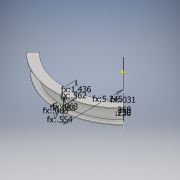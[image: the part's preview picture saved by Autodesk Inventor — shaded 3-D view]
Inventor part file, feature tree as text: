
AUTODESK INVENTOR PART (.ipt)
format: ipt  version: 2017 (Build 210142000, 142)  size: 168,448 bytes
history: native  units: in
note: dims shown in document units (in); Inventor stores cm internally (conversion verified against a paired STEP export)
features: sketch x5, extrude x4, revolve x1, plane x1
ambient origin geometry x8: Origin, YZ Plane, XZ Plane, XY Plane, X Axis, Y Axis, Z Axis, Center Point
bodies: Solid1 (feature_tree)
feature tree (11):
  revolve  "Revolution1"  [1 undecoded]
  plane  "Work Plane1"
  sketch  "Sketch2"  dims[d3=1.4364in d4=0.0625in]
  extrude  "Extrusion2"  Depth=0.0625in
  extrude  "Extrusion3"  TaperAngle=90.0deg  [1 undecoded]
  extrude  "Extrusion4"  Depth=0.375in
  extrude  "Extrusion5"  Depth=0.0312in TaperAngle=0.0deg
  sketch  "Sketch5"  dims[d11=0.3125in d12=1.0in d13=0.0in d14=0.0156in d15=0.0in d16=0.25in d17=0.0625in d18=0.0in d19=135.0deg d20=0.0in d21=0.0in d22=0.75in d23=0.0312in d24=0.25in d25=0.25in]
  sketch  "Sketch1"  dims[d1=0.5536in d2=0.0625in]
  sketch  "Sketch3"  dims[d5=0.0625in d6=90.0deg]
  sketch  "Sketch4"  dims[d7=0.562in d8=0.375in]
note: 2 required parameter values undecoded (feature->parameter linkage not recoverable at this tier; creation-order binding heuristic only, values carry confidence <= 0.55)